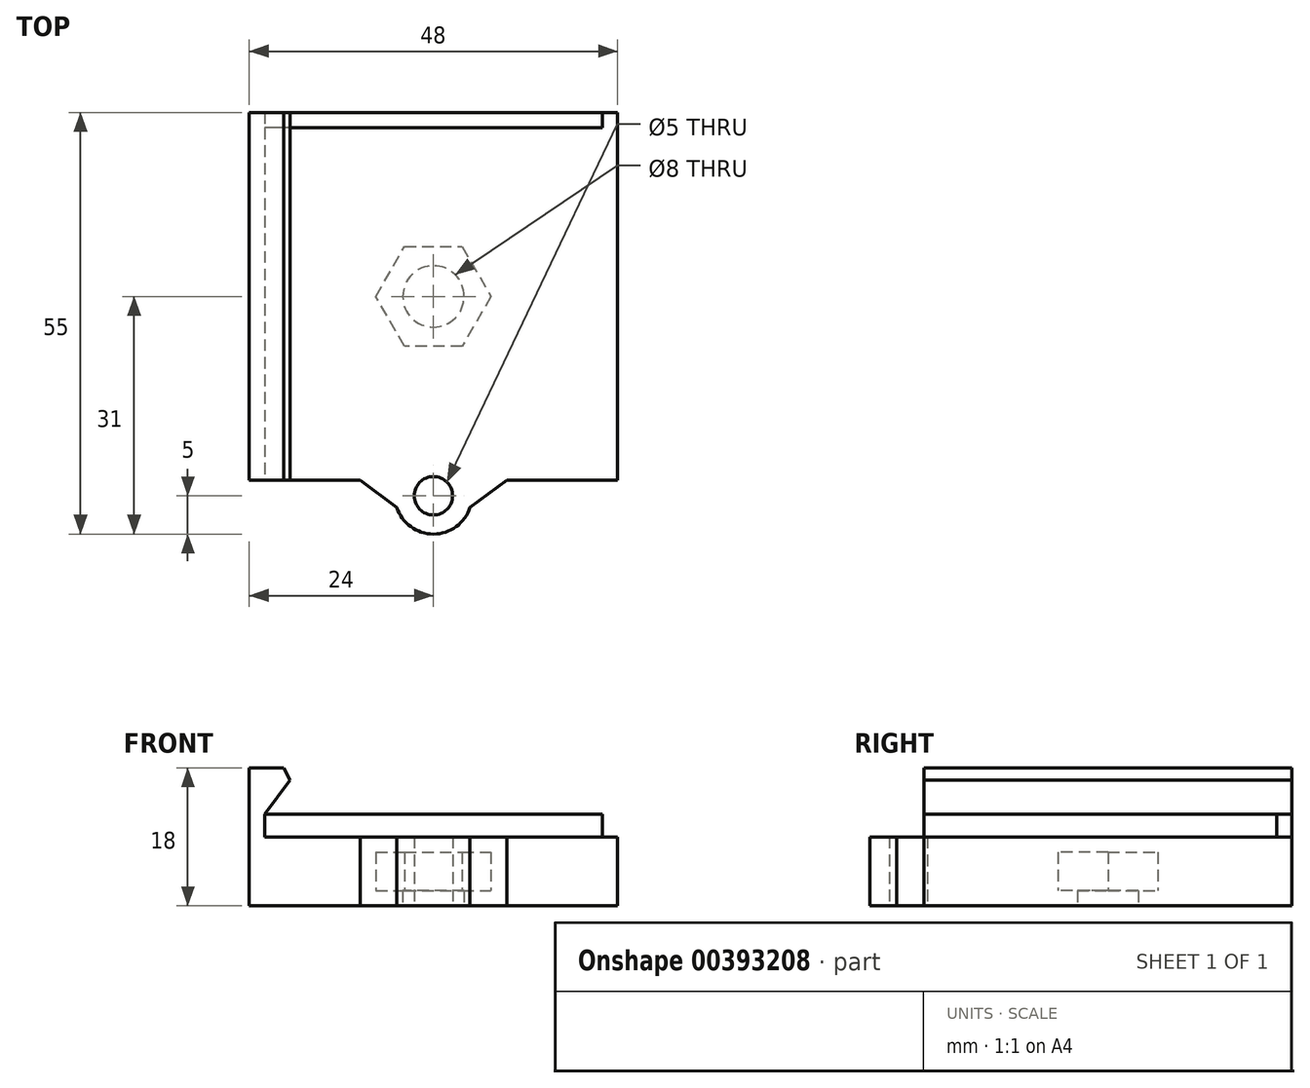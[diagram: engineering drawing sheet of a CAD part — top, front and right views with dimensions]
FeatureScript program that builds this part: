
annotation { "Feature Type Name" : "Feature", "Feature Type Description" : "" }
export const myFeature = defineFeature(function(context is Context, id is Id, definition is map)
    precondition{}
    {
        {
            var Q0;
            Q0=qCreatedBy(makeId("Top.planeOp"),FACE);
            var sketch = newSketch(context, id + "F0", { "sketchPlane" : qUnion([Q0])});
            skLineSegment(sketch, "E0.bottom", {"start": v(24, 24) * mm, "end": v(-24, 24) * mm});
            skLineSegment(sketch, "E0.top", {"start": v(24, -24) * mm, "end": v(-24, -24) * mm});
            skLineSegment(sketch, "E0.left", {"start": v(24, 24) * mm, "end": v(24, -24) * mm});
            skLineSegment(sketch, "E0.right", {"start": v(-24, 24) * mm, "end": v(-24, -24) * mm});
            skPoint(sketch, "E0.middle", {"position": v(0, 0) * mm});
            skCircle(sketch, "E1.cCircle", {"center": v(0, 0) * mm, "radius": 6.5 * mm, "construction": true});
            skLineSegment(sketch, "E1.0", {"start": v(-3.75, 6.5) * mm, "end": v(3.75, 6.5) * mm});
            skLineSegment(sketch, "E1.1", {"start": v(3.75, 6.5) * mm, "end": v(7.5, 0) * mm});
            skLineSegment(sketch, "E1.2", {"start": v(7.5, 0) * mm, "end": v(3.75, -6.5) * mm});
            skLineSegment(sketch, "E1.3", {"start": v(3.75, -6.5) * mm, "end": v(-3.75, -6.5) * mm});
            skLineSegment(sketch, "E1.4", {"start": v(-3.75, -6.5) * mm, "end": v(-7.5, 0) * mm});
            skLineSegment(sketch, "E1.5", {"start": v(-7.5, 0) * mm, "end": v(-3.75, 6.5) * mm});
            skPoint(sketch, "E1.0.midPoint", {"position": v(0, 6.5) * mm});
            skCircle(sketch, "E2", {"center": v(0, 0) * mm, "radius": 4 * mm});
            skLineSegment(sketch, "E3", {"start": v(5, -24) * mm, "end": v(5, -28) * mm});
            skLineSegment(sketch, "E4.MirrorCS", {"start": v(-5, -24) * mm, "end": v(-5, -28) * mm});
            skArc(sketch, "E5", {"start": v(-5, -26) * mm, "mid": v(0, -31) * mm, "end": v(5, -26) * mm});
            skCircle(sketch, "E6", {"center": v(0, -26) * mm, "radius": 2.5 * mm});
            skSolve(sketch);
        }
        {
            var Q0;
            Q0 = qSketchRegion(id + "F0", true);
            extrude(context, id + "F1", {"entities" : qUnion([Q0]), "depth" : 7 * mm});
        }
        {
            var Q0;
            Q0=makeQuery(id+"F0.imprint","IMPRINT",FACE,{"disambiguationData":[TD([[makeQuery(id+"F0.imprint","IMPRINT",EDGE,{"derivedFrom":sQuery(id+"F0.wireOp",EDGE,"E1.0")}),-1.0]])]});
            extrude(context, id + "F2", {"entities" : qUnion([Q0]), "operationType" : NewBodyOperationType.ADD, "depth" : 2 * mm});
        }
        {
            var Q0;
            Q0=makeQuery(id+"F1.opExtrude","CAP_FACE",FACE,{"disambiguationData":[OSD([sQuery(id+"F0.wireOp",EDGE,"E0.bottom"),sQuery(id+"F0.wireOp",EDGE,"E0.top"),sQuery(id+"F0.wireOp",EDGE,"E0.left"),sQuery(id+"F0.wireOp",EDGE,"E0.right"),sQuery(id+"F0.wireOp",EDGE,"E1.0"),sQuery(id+"F0.wireOp",EDGE,"E1.1"),sQuery(id+"F0.wireOp",EDGE,"E1.2"),sQuery(id+"F0.wireOp",EDGE,"E1.3"),sQuery(id+"F0.wireOp",EDGE,"E1.4"),sQuery(id+"F0.wireOp",EDGE,"E1.5")])],"isStart":false});
            var sketch = newSketch(context, id + "F3", { "sketchPlane" : qUnion([Q0])});
            skLineSegment(sketch, "E7.bottom", {"start": v(-24, 24) * mm, "end": v(24, 24) * mm});
            skLineSegment(sketch, "E7.top", {"start": v(-24, -24) * mm, "end": v(24, -24) * mm});
            skLineSegment(sketch, "E7.left", {"start": v(-24, 24) * mm, "end": v(-24, -24) * mm});
            skLineSegment(sketch, "E7.right", {"start": v(24, 24) * mm, "end": v(24, -24) * mm});
            skSolve(sketch);
        }
        {
            var Q0;
            Q0=makeQuery(id+"F3.imprint","IMPRINT",FACE,{"disambiguationData":[TD([[makeQuery(id+"F3.imprint","IMPRINT",EDGE,{"derivedFrom":makeQuery(id+"F1.opExtrude","CAP_EDGE",EDGE,{"disambiguationData":[OSD([sQuery(id+"F0.wireOp",EDGE,"E1.0")])],"isStart":false})}),-1.0]])]});
            var Q1;
            Q1=makeQuery(id+"F3.imprint","IMPRINT",FACE,{"disambiguationData":[TD([[makeQuery(id+"F3.imprint","IMPRINT",EDGE,{"derivedFrom":sQuery(id+"F3.wireOp",EDGE,"E7.bottom")}),1.0]])]});
            extrude(context, id + "F4", {"entities" : qUnion([Q0, Q1]), "operationType" : NewBodyOperationType.ADD, "depth" : 2 * mm});
        }
        {
            var Q0;
            Q0=makeQuery(id+"F4.boolean.opBoolean","MERGE",FACE,{"derivedFrom":[makeQuery(id+"F1.opExtrude","SWEPT_FACE",FACE,{"disambiguationData":[OSD([sQuery(id+"F0.wireOp",EDGE,"E0.top")])]}),makeQuery(id+"F4.opExtrude","SWEPT_FACE",FACE,{"disambiguationData":[OSD([sQuery(id+"F3.wireOp",EDGE,"E7.top")])]})]});
            var sketch = newSketch(context, id + "F5", { "sketchPlane" : qUnion([Q0])});
            skLineSegment(sketch, "E8", {"start": v(24, 9) * mm, "end": v(24, 18) * mm});
            skLineSegment(sketch, "E9", {"start": v(24, 18) * mm, "end": v(17.5, 18) * mm});
            skLineSegment(sketch, "E10.0", {"start": v(22, 9) * mm, "end": v(22, 12) * mm});
            skLineSegment(sketch, "E11", {"start": v(22, 12) * mm, "end": v(17.5, 18) * mm});
            skLineSegment(sketch, "E12.MirrorCS", {"start": v(-22, 9) * mm, "end": v(-22, 12) * mm});
            skLineSegment(sketch, "E13.MirrorCS", {"start": v(-22, 12) * mm, "end": v(-17.5, 18) * mm});
            skLineSegment(sketch, "E14.MirrorCS", {"start": v(-24, 9) * mm, "end": v(-24, 18) * mm});
            skLineSegment(sketch, "E15.MirrorCS", {"start": v(-24, 18) * mm, "end": v(-17.5, 18) * mm});
            skSolve(sketch);
        }
        {
            var Q0;
            {var subQ1=sQuery(id+"F5.wireOp",EDGE,"E12.MirrorCS");Q0=makeQuery(id+"F5.imprint","IMPRINT",FACE,{"disambiguationData":[TD([[makeQuery(id+"F5.imprint","IMPRINT",EDGE,{"derivedFrom":subQ1}),1.0]])]});}
            var Q1;
            {var subQ1=sQuery(id+"F5.wireOp",EDGE,"E8");Q1=makeQuery(id+"F5.imprint","IMPRINT",FACE,{"disambiguationData":[TD([[makeQuery(id+"F5.imprint","IMPRINT",EDGE,{"derivedFrom":subQ1}),1.0]])]});}
            extrude(context, id + "F6", {"entities" : qUnion([Q0, Q1]), "operationType" : NewBodyOperationType.ADD, "oppositeDirection" : true, "depth" : 48 * mm});
        }
        {
            var Q0;
            Q0=makeQuery(id+"F4.opExtrude","CAP_FACE",FACE,{"disambiguationData":[OSD([sQuery(id+"F3.wireOp",EDGE,"E7.bottom"),sQuery(id+"F3.wireOp",EDGE,"E7.top"),sQuery(id+"F3.wireOp",EDGE,"E7.left"),sQuery(id+"F3.wireOp",EDGE,"E7.right")])],"isStart":false});
            var sketch = newSketch(context, id + "F7", { "sketchPlane" : qUnion([Q0])});
            skLineSegment(sketch, "E16.bottom", {"start": v(22, 24) * mm, "end": v(-22, 24) * mm});
            skLineSegment(sketch, "E16.top", {"start": v(22, 22) * mm, "end": v(-22, 22) * mm});
            skLineSegment(sketch, "E16.left", {"start": v(22, 24) * mm, "end": v(22, 22) * mm});
            skLineSegment(sketch, "E16.right", {"start": v(-22, 24) * mm, "end": v(-22, 22) * mm});
            skSolve(sketch);
        }
        {
            var Q0;
            {var subQ4=sQuery(id+"F7.wireOp",EDGE,"E16.right");Q0=makeQuery(id+"F7.imprint","IMPRINT",FACE,{"disambiguationData":[TD([[makeQuery(id+"F7.imprint","IMPRINT",EDGE,{"derivedFrom":subQ4}),1.0]])]});}
            extrude(context, id + "F8", {"entities" : qUnion([Q0]), "operationType" : NewBodyOperationType.ADD, "depth" : 3 * mm});
        }
        {
            var Q0;
            {var subQ3=sQuery(id+"F7.wireOp",EDGE,"E16.left");Q0=makeQuery(id+"F7.imprint","IMPRINT",FACE,{"disambiguationData":[TD([[makeQuery(id+"F7.imprint","IMPRINT",EDGE,{"derivedFrom":subQ3}),-1.0]])]});}
            var Q1;
            {var subQ4=sQuery(id+"F7.wireOp",EDGE,"E16.right");Q1=makeQuery(id+"F7.imprint","IMPRINT",FACE,{"disambiguationData":[TD([[makeQuery(id+"F7.imprint","IMPRINT",EDGE,{"derivedFrom":subQ4}),1.0]])]});}
            var Q2;
            Q2=makeQuery(id+"F7.imprint","IMPRINT",FACE,{"disambiguationData":[TD([[makeQuery(id+"F7.imprint","IMPRINT",EDGE,{"derivedFrom":sQuery(id+"F7.wireOp",EDGE,"kU60GswA-P6Qy-dfav-r5oV-xm8rNlg5Zm60")}),1.0]])]});
            var Q3;
            Q3=makeQuery(id+"F7.imprint","IMPRINT",FACE,{"disambiguationData":[TD([[makeQuery(id+"F7.imprint","IMPRINT",EDGE,{"derivedFrom":sQuery(id+"F7.wireOp",EDGE,"2e802822-9bce-4a6b-b7d6-acc537c387130.MirrorC")}),-1.0]])]});
            var Q4;
            Q4=makeQuery(id+"F7.imprint","IMPRINT",FACE,{"disambiguationData":[TD([[makeQuery(id+"F7.imprint","IMPRINT",EDGE,{"derivedFrom":sQuery(id+"F7.wireOp",EDGE,"54062cb7-d33c-4621-ad21-35ebbc401f7b.1.0.0")}),1.0]])]});
            extrude(context, id + "F9", {"entities" : qUnion([Q0, Q1, Q2, Q3, Q4]), "operationType" : NewBodyOperationType.ADD, "depth" : 1 * mm});
        }
        {
            var Q0;
            Q0=makeQuery(id+"F6.opExtrude","SWEPT_EDGE",EDGE,{"disambiguationData":[OSD([sQuery(id+"F5.wireOp",EDGE,"E9"),sQuery(id+"F5.wireOp",EDGE,"E11")])]});
            var Q1;
            Q1=makeQuery(id+"F6.opExtrude","SWEPT_EDGE",EDGE,{"disambiguationData":[OSD([sQuery(id+"F5.wireOp",EDGE,"E13.MirrorCS"),sQuery(id+"F5.wireOp",EDGE,"E15.MirrorCS")])]});
            chamfer(context, id + "F10", {"entities" : qUnion([Q0, Q1]), "width" : 1 * mm, "tangentPropagation" : true});
        }
        {
            var Q0;
            Q0=makeQuery(id+"F1.opExtrude","SWEPT_EDGE",EDGE,{"disambiguationData":[OSD([sQuery(id+"F0.wireOp",EDGE,"E0.top"),sQuery(id+"F0.wireOp",EDGE,"E4.MirrorCS")])]});
            var Q1;
            Q1=makeQuery(id+"F1.opExtrude","SWEPT_EDGE",EDGE,{"disambiguationData":[OSD([sQuery(id+"F0.wireOp",EDGE,"E0.top"),sQuery(id+"F0.wireOp",EDGE,"E3")])]});
            chamfer(context, id + "F11", {"entities" : qUnion([Q0, Q1]), "width" : 5 * mm, "tangentPropagation" : true});
        }
        {
            var Q0;
            Q0=makeQuery(id+"F1.opExtrude","CAP_FACE",FACE,{"disambiguationData":[OSD([sQuery(id+"F0.wireOp",EDGE,"E0.bottom"),sQuery(id+"F0.wireOp",EDGE,"E0.top"),sQuery(id+"F0.wireOp",EDGE,"E0.left"),sQuery(id+"F0.wireOp",EDGE,"E0.right"),sQuery(id+"F0.wireOp",EDGE,"E1.0"),sQuery(id+"F0.wireOp",EDGE,"E1.1"),sQuery(id+"F0.wireOp",EDGE,"E1.2"),sQuery(id+"F0.wireOp",EDGE,"E1.3"),sQuery(id+"F0.wireOp",EDGE,"E1.4"),sQuery(id+"F0.wireOp",EDGE,"E1.5"),sQuery(id+"F0.wireOp",EDGE,"E3"),sQuery(id+"F0.wireOp",EDGE,"E4.MirrorCS"),sQuery(id+"F0.wireOp",EDGE,"E5"),sQuery(id+"F0.wireOp",EDGE,"E6")])],"isStart":false});
            extrude(context, id + "F12", {"entities" : qUnion([Q0]), "operationType" : NewBodyOperationType.ADD, "depth" : 2 * mm});
        }
    });
